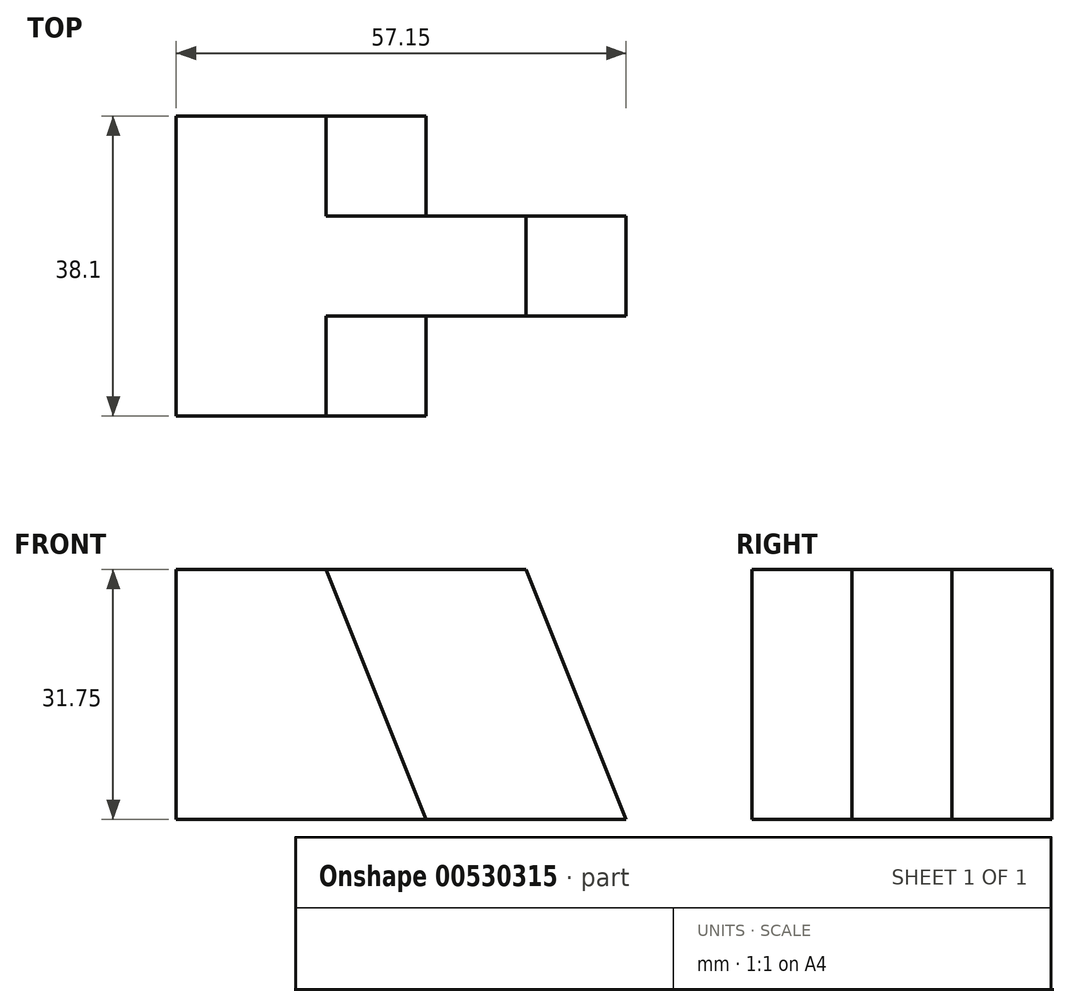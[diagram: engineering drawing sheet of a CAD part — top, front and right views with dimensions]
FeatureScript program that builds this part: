
annotation { "Feature Type Name" : "Feature", "Feature Type Description" : "" }
export const myFeature = defineFeature(function(context is Context, id is Id, definition is map)
    precondition{}
    {
        {
            var Q0;
            Q0=qCreatedBy(makeId("Front.planeOp"),FACE);
            var sketch = newSketch(context, id + "F0", { "sketchPlane" : qUnion([Q0])});
            skLineSegment(sketch, "E0", {"start": v(-76.2, 0) * mm, "end": v(-19.05, 0) * mm});
            skLineSegment(sketch, "E1", {"start": v(-76.2, 0) * mm, "end": v(-76.2, 31.75) * mm});
            skLineSegment(sketch, "E2", {"start": v(-76.2, 31.75) * mm, "end": v(-19.05, 31.75) * mm});
            skLineSegment(sketch, "E3", {"start": v(-19.05, 31.75) * mm, "end": v(-19.05, 0) * mm});
            skSolve(sketch);
        }
        {
            var Q0;
            Q0=makeQuery(id+"F0.imprint","IMPRINT",FACE,{"disambiguationData":[TD([[makeQuery(id+"F0.imprint","IMPRINT",EDGE,{"derivedFrom":sQuery(id+"F0.wireOp",EDGE,"E0")}),1.0]])]});
            extrude(context, id + "F1", {"entities" : qUnion([Q0]), "depth" : 38.1 * mm, "offsetDistance" : 25.4 * mm});
        }
        {
            var Q0;
            Q0=makeQuery(id+"F1.opExtrude","CAP_FACE",FACE,{"disambiguationData":[OSD([sQuery(id+"F0.wireOp",EDGE,"E0"),sQuery(id+"F0.wireOp",EDGE,"E1"),sQuery(id+"F0.wireOp",EDGE,"E2"),sQuery(id+"F0.wireOp",EDGE,"E3")])],"isStart":false});
            var sketch = newSketch(context, id + "F2", { "sketchPlane" : qUnion([Q0])});
            skLineSegment(sketch, "E4", {"start": v(-19.05, 0) * mm, "end": v(-44.45, 0) * mm});
            skLineSegment(sketch, "E5", {"start": v(-19.05, 31.75) * mm, "end": v(-31.75, 31.75) * mm});
            skLineSegment(sketch, "E6", {"start": v(-19.05, 0) * mm, "end": v(-31.75, 31.75) * mm});
            skSolve(sketch);
        }
        {
            var Q0;
            Q0=makeQuery(id+"F2.imprint","IMPRINT",FACE,{"disambiguationData":[TD([[makeQuery(id+"F2.imprint","IMPRINT",EDGE,{"derivedFrom":sQuery(id+"F2.wireOp",EDGE,"E5")}),-1.0]])]});
            extrude(context, id + "F3", {"entities" : qUnion([Q0]), "operationType" : NewBodyOperationType.REMOVE, "endBound" : BoundingType.THROUGH_ALL, "oppositeDirection" : true, "depth" : 25.4 * mm, "offsetDistance" : 25.4 * mm});
        }
        {
            var Q0;
            Q0=makeQuery(id+"F1.opExtrude","CAP_FACE",FACE,{"disambiguationData":[OSD([sQuery(id+"F0.wireOp",EDGE,"E0"),sQuery(id+"F0.wireOp",EDGE,"E1"),sQuery(id+"F0.wireOp",EDGE,"E2"),sQuery(id+"F0.wireOp",EDGE,"E3")])],"isStart":false});
            var sketch = newSketch(context, id + "F4", { "sketchPlane" : qUnion([Q0])});
            skLineSegment(sketch, "E7", {"start": v(-19.05, 0) * mm, "end": v(-44.45, 0) * mm});
            skLineSegment(sketch, "E8", {"start": v(-31.75, 31.75) * mm, "end": v(-57.15, 31.75) * mm});
            skLineSegment(sketch, "E9", {"start": v(-57.15, 31.75) * mm, "end": v(-44.45, 0) * mm});
            skSolve(sketch);
        }
        {
            var Q0;
            Q0=makeQuery(id+"F4.imprint","IMPRINT",FACE,{"disambiguationData":[TD([[makeQuery(id+"F4.imprint","IMPRINT",EDGE,{"derivedFrom":sQuery(id+"F4.wireOp",EDGE,"E7")}),1.0]])]});
            extrude(context, id + "F5", {"entities" : qUnion([Q0]), "operationType" : NewBodyOperationType.REMOVE, "oppositeDirection" : true, "depth" : 12.7 * mm, "offsetDistance" : 25.4 * mm});
        }
        {
            var Q0;
            Q0=makeQuery(id+"F1.opExtrude","CAP_FACE",FACE,{"disambiguationData":[OSD([sQuery(id+"F0.wireOp",EDGE,"E0"),sQuery(id+"F0.wireOp",EDGE,"E1"),sQuery(id+"F0.wireOp",EDGE,"E2"),sQuery(id+"F0.wireOp",EDGE,"E3")])],"isStart":true});
            var sketch = newSketch(context, id + "F6", { "sketchPlane" : qUnion([Q0])});
            skLineSegment(sketch, "E10", {"start": v(19.05, 0) * mm, "end": v(44.45, 0) * mm});
            skLineSegment(sketch, "E11", {"start": v(31.75, 31.75) * mm, "end": v(57.15, 31.75) * mm});
            skLineSegment(sketch, "E12", {"start": v(44.45, 0) * mm, "end": v(57.15, 31.75) * mm});
            skSolve(sketch);
        }
        {
            var Q0;
            Q0=makeQuery(id+"F6.imprint","IMPRINT",FACE,{"disambiguationData":[TD([[makeQuery(id+"F6.imprint","IMPRINT",EDGE,{"derivedFrom":sQuery(id+"F6.wireOp",EDGE,"E10")}),-1.0]])]});
            extrude(context, id + "F7", {"entities" : qUnion([Q0]), "operationType" : NewBodyOperationType.REMOVE, "oppositeDirection" : true, "depth" : 12.7 * mm, "offsetDistance" : 25.4 * mm});
        }
    });
